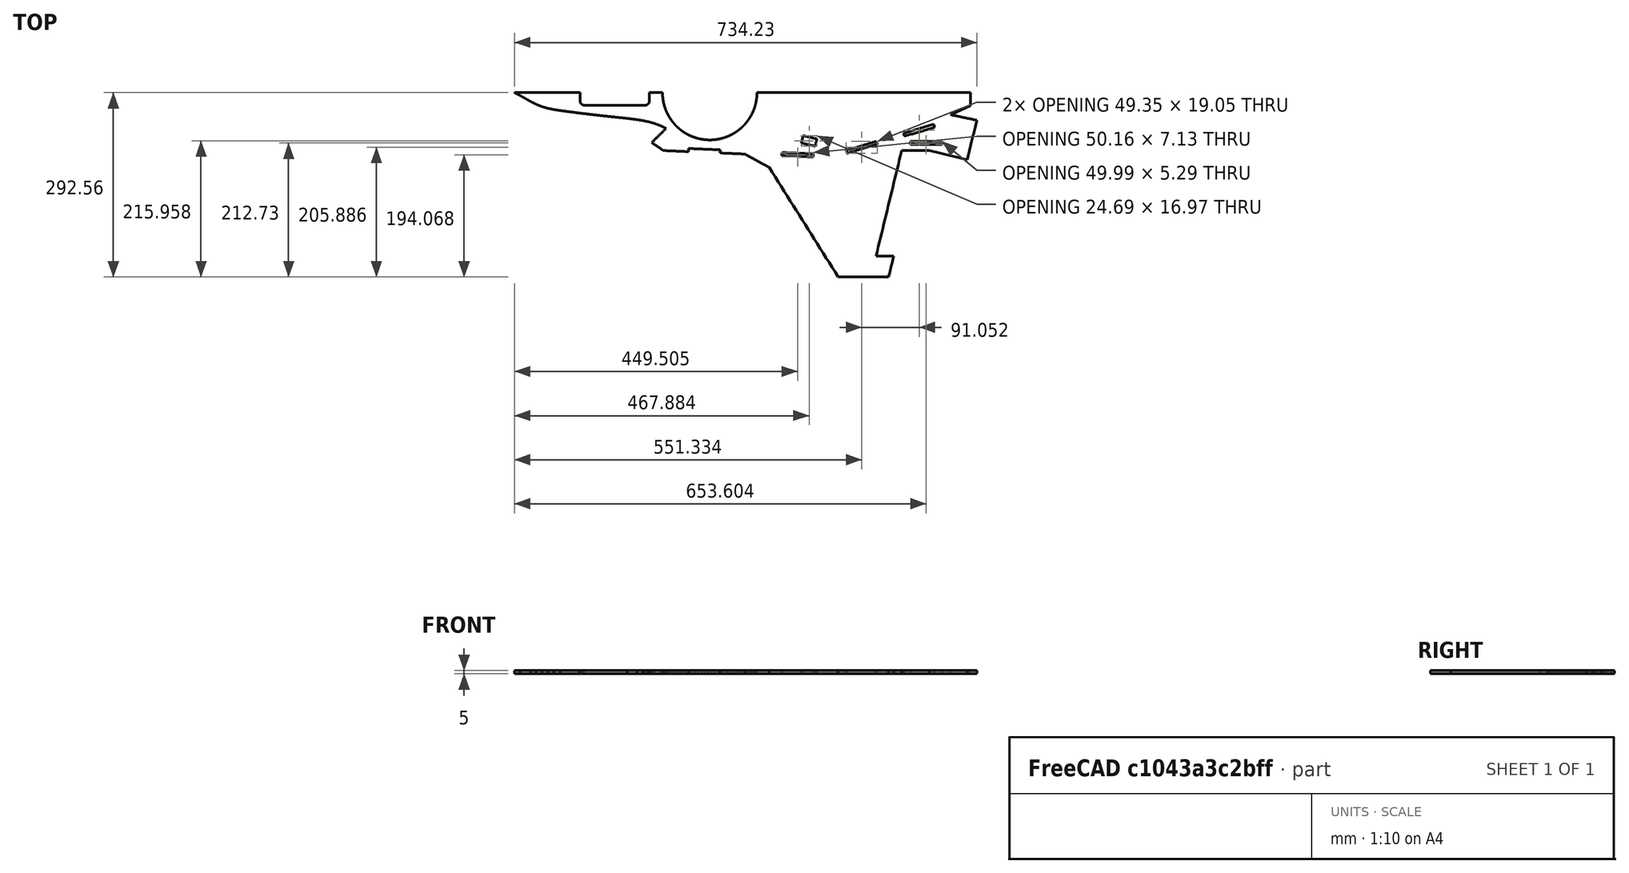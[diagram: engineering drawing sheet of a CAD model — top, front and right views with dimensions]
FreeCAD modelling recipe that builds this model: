
FCSTD DOCUMENT  (FreeCAD 0.19R)
Label: F-35_v2_parts_13
License: All rights reserved
LicenseURL: http://en.wikipedia.org/wiki/All_rights_reserved
objects: PartDesign::CoordinateSystem×7, App::DocumentObjectGroup×2, App::FeaturePython×1, Sketcher::SketchObject×1, PartDesign::Pad×1, PartDesign::Body×1, App::Part×1
note: 11 computed .brp shape members not serialized (recipe doc carries the construction recipe); baked Part::Feature solids carry a one-line shape summary decoded from their .brp

FEATURE [App::DocumentObjectGroup] Parts
FEATURE [PartDesign::CoordinateSystem] LCS_Origin
  AttacherType = Attacher::AttachEngine3D
  MapMode = 2
  Support = -> [X_Axis]
FEATURE [App::DocumentObjectGroup] Constraints
FEATURE [App::FeaturePython] Variables  # WARN: FeaturePython — macro-defined, semantics opaque (R4)
FEATURE [Sketcher::SketchObject] Sketch
  FullyConstrained = false
  sketch-geometry (125):
    g0: BSplineCurve PolesCount=2 KnotsCount=2 Degree=1 IsPeriodic=0
    g1: BSplineCurve PolesCount=2 KnotsCount=2 Degree=1 IsPeriodic=0
    g2: BSplineCurve PolesCount=2 KnotsCount=2 Degree=1 IsPeriodic=0
    g3: BSplineCurve PolesCount=2 KnotsCount=2 Degree=1 IsPeriodic=0
    g4: BSplineCurve PolesCount=2 KnotsCount=2 Degree=1 IsPeriodic=0
    g5: BSplineCurve PolesCount=2 KnotsCount=2 Degree=1 IsPeriodic=0
    g6: BSplineCurve PolesCount=2 KnotsCount=2 Degree=1 IsPeriodic=0
    g7: BSplineCurve PolesCount=2 KnotsCount=2 Degree=1 IsPeriodic=0
    g8: BSplineCurve PolesCount=2 KnotsCount=2 Degree=1 IsPeriodic=0
    g9: BSplineCurve PolesCount=2 KnotsCount=2 Degree=1 IsPeriodic=0
    g10: BSplineCurve PolesCount=2 KnotsCount=2 Degree=1 IsPeriodic=0
    g11: BSplineCurve PolesCount=2 KnotsCount=2 Degree=1 IsPeriodic=0
    g12: BSplineCurve PolesCount=2 KnotsCount=2 Degree=1 IsPeriodic=0
    g13: BSplineCurve PolesCount=2 KnotsCount=2 Degree=1 IsPeriodic=0
    g14: BSplineCurve PolesCount=2 KnotsCount=2 Degree=1 IsPeriodic=0
    g15: BSplineCurve PolesCount=2 KnotsCount=2 Degree=1 IsPeriodic=0
    g16: BSplineCurve PolesCount=2 KnotsCount=2 Degree=1 IsPeriodic=0
    g17: BSplineCurve PolesCount=2 KnotsCount=2 Degree=1 IsPeriodic=0
    g18: BSplineCurve PolesCount=2 KnotsCount=2 Degree=1 IsPeriodic=0
    g19: BSplineCurve PolesCount=2 KnotsCount=2 Degree=1 IsPeriodic=0
    g20: BSplineCurve PolesCount=2 KnotsCount=2 Degree=1 IsPeriodic=0
    g21: BSplineCurve PolesCount=2 KnotsCount=2 Degree=1 IsPeriodic=0
    g22: BSplineCurve PolesCount=2 KnotsCount=2 Degree=1 IsPeriodic=0
    g23: BSplineCurve PolesCount=2 KnotsCount=2 Degree=1 IsPeriodic=0
    g24: BSplineCurve PolesCount=2 KnotsCount=2 Degree=1 IsPeriodic=0
    g25: BSplineCurve PolesCount=2 KnotsCount=2 Degree=1 IsPeriodic=0
    g26: BSplineCurve PolesCount=2 KnotsCount=2 Degree=1 IsPeriodic=0
    g27: BSplineCurve PolesCount=2 KnotsCount=2 Degree=1 IsPeriodic=0
    g28: BSplineCurve PolesCount=2 KnotsCount=2 Degree=1 IsPeriodic=0
    g29: BSplineCurve PolesCount=2 KnotsCount=2 Degree=1 IsPeriodic=0
    g30: BSplineCurve PolesCount=2 KnotsCount=2 Degree=1 IsPeriodic=0
    g31: BSplineCurve PolesCount=2 KnotsCount=2 Degree=1 IsPeriodic=0
    g32: BSplineCurve PolesCount=2 KnotsCount=2 Degree=1 IsPeriodic=0
    g33: BSplineCurve PolesCount=2 KnotsCount=2 Degree=1 IsPeriodic=0
    g34: BSplineCurve PolesCount=2 KnotsCount=2 Degree=1 IsPeriodic=0
    g35: BSplineCurve PolesCount=2 KnotsCount=2 Degree=1 IsPeriodic=0
    g36: BSplineCurve PolesCount=2 KnotsCount=2 Degree=1 IsPeriodic=0
    g37: BSplineCurve PolesCount=2 KnotsCount=2 Degree=1 IsPeriodic=0
    g38: BSplineCurve PolesCount=2 KnotsCount=2 Degree=1 IsPeriodic=0
    g39: BSplineCurve PolesCount=2 KnotsCount=2 Degree=1 IsPeriodic=0
    g40: BSplineCurve PolesCount=2 KnotsCount=2 Degree=1 IsPeriodic=0
    g41: BSplineCurve PolesCount=2 KnotsCount=2 Degree=1 IsPeriodic=0
    g42: BSplineCurve PolesCount=2 KnotsCount=2 Degree=1 IsPeriodic=0
    g43: BSplineCurve PolesCount=2 KnotsCount=2 Degree=1 IsPeriodic=0
    g44: BSplineCurve PolesCount=2 KnotsCount=2 Degree=1 IsPeriodic=0
    g45: BSplineCurve PolesCount=2 KnotsCount=2 Degree=1 IsPeriodic=0
    g46: BSplineCurve PolesCount=2 KnotsCount=2 Degree=1 IsPeriodic=0
    g47: BSplineCurve PolesCount=2 KnotsCount=2 Degree=1 IsPeriodic=0
    g48: BSplineCurve PolesCount=2 KnotsCount=2 Degree=1 IsPeriodic=0
    g49: BSplineCurve PolesCount=2 KnotsCount=2 Degree=1 IsPeriodic=0
    g50: BSplineCurve PolesCount=2 KnotsCount=2 Degree=1 IsPeriodic=0
    g51: BSplineCurve PolesCount=2 KnotsCount=2 Degree=1 IsPeriodic=0
    g52: BSplineCurve PolesCount=2 KnotsCount=2 Degree=1 IsPeriodic=0
    g53: BSplineCurve PolesCount=2 KnotsCount=2 Degree=1 IsPeriodic=0
    g54: BSplineCurve PolesCount=2 KnotsCount=2 Degree=1 IsPeriodic=0
    g55: BSplineCurve PolesCount=2 KnotsCount=2 Degree=1 IsPeriodic=0
    g56: BSplineCurve PolesCount=2 KnotsCount=2 Degree=1 IsPeriodic=0
    g57: BSplineCurve PolesCount=2 KnotsCount=2 Degree=1 IsPeriodic=0
    g58: BSplineCurve PolesCount=2 KnotsCount=2 Degree=1 IsPeriodic=0
    g59: BSplineCurve PolesCount=2 KnotsCount=2 Degree=1 IsPeriodic=0
    g60: BSplineCurve PolesCount=2 KnotsCount=2 Degree=1 IsPeriodic=0
    g61: BSplineCurve PolesCount=2 KnotsCount=2 Degree=1 IsPeriodic=0
    g62: BSplineCurve PolesCount=2 KnotsCount=2 Degree=1 IsPeriodic=0
    g63: BSplineCurve PolesCount=2 KnotsCount=2 Degree=1 IsPeriodic=0
    g64: BSplineCurve PolesCount=2 KnotsCount=2 Degree=1 IsPeriodic=0
    g65: BSplineCurve PolesCount=2 KnotsCount=2 Degree=1 IsPeriodic=0
    g66: BSplineCurve PolesCount=2 KnotsCount=2 Degree=1 IsPeriodic=0
    g67: BSplineCurve PolesCount=2 KnotsCount=2 Degree=1 IsPeriodic=0
    g68: BSplineCurve PolesCount=2 KnotsCount=2 Degree=1 IsPeriodic=0
    g69: BSplineCurve PolesCount=2 KnotsCount=2 Degree=1 IsPeriodic=0
    g70: BSplineCurve PolesCount=2 KnotsCount=2 Degree=1 IsPeriodic=0
    g71: BSplineCurve PolesCount=2 KnotsCount=2 Degree=1 IsPeriodic=0
    g72: BSplineCurve PolesCount=2 KnotsCount=2 Degree=1 IsPeriodic=0
    g73: BSplineCurve PolesCount=2 KnotsCount=2 Degree=1 IsPeriodic=0
    g74: BSplineCurve PolesCount=2 KnotsCount=2 Degree=1 IsPeriodic=0
    g75: BSplineCurve PolesCount=2 KnotsCount=2 Degree=1 IsPeriodic=0
    g76: BSplineCurve PolesCount=2 KnotsCount=2 Degree=1 IsPeriodic=0
    g77: BSplineCurve PolesCount=2 KnotsCount=2 Degree=1 IsPeriodic=0
    g78: BSplineCurve PolesCount=2 KnotsCount=2 Degree=1 IsPeriodic=0
    g79: BSplineCurve PolesCount=2 KnotsCount=2 Degree=1 IsPeriodic=0
    g80: BSplineCurve PolesCount=2 KnotsCount=2 Degree=1 IsPeriodic=0
    g81: BSplineCurve PolesCount=2 KnotsCount=2 Degree=1 IsPeriodic=0
    g82: BSplineCurve PolesCount=2 KnotsCount=2 Degree=1 IsPeriodic=0
    g83: BSplineCurve PolesCount=2 KnotsCount=2 Degree=1 IsPeriodic=0
    g84: BSplineCurve PolesCount=2 KnotsCount=2 Degree=1 IsPeriodic=0
    g85: BSplineCurve PolesCount=2 KnotsCount=2 Degree=1 IsPeriodic=0
    g86: BSplineCurve PolesCount=2 KnotsCount=2 Degree=1 IsPeriodic=0
    g87: BSplineCurve PolesCount=2 KnotsCount=2 Degree=1 IsPeriodic=0
    g88: BSplineCurve PolesCount=2 KnotsCount=2 Degree=1 IsPeriodic=0
    g89: BSplineCurve PolesCount=2 KnotsCount=2 Degree=1 IsPeriodic=0
    g90: BSplineCurve PolesCount=2 KnotsCount=2 Degree=1 IsPeriodic=0
    g91: BSplineCurve PolesCount=2 KnotsCount=2 Degree=1 IsPeriodic=0
    g92: BSplineCurve PolesCount=2 KnotsCount=2 Degree=1 IsPeriodic=0
    g93: BSplineCurve PolesCount=2 KnotsCount=2 Degree=1 IsPeriodic=0
    g94: BSplineCurve PolesCount=2 KnotsCount=2 Degree=1 IsPeriodic=0
    g95: BSplineCurve PolesCount=2 KnotsCount=2 Degree=1 IsPeriodic=0
    g96: BSplineCurve PolesCount=2 KnotsCount=2 Degree=1 IsPeriodic=0
    g97: BSplineCurve PolesCount=2 KnotsCount=2 Degree=1 IsPeriodic=0
    g98: BSplineCurve PolesCount=2 KnotsCount=2 Degree=1 IsPeriodic=0
    g99: BSplineCurve PolesCount=2 KnotsCount=2 Degree=1 IsPeriodic=0
    g100: BSplineCurve PolesCount=2 KnotsCount=2 Degree=1 IsPeriodic=0
    g101: BSplineCurve PolesCount=2 KnotsCount=2 Degree=1 IsPeriodic=0
    g102: BSplineCurve PolesCount=2 KnotsCount=2 Degree=1 IsPeriodic=0
    g103: BSplineCurve PolesCount=2 KnotsCount=2 Degree=1 IsPeriodic=0
    g104: BSplineCurve PolesCount=2 KnotsCount=2 Degree=1 IsPeriodic=0
    g105: BSplineCurve PolesCount=2 KnotsCount=2 Degree=1 IsPeriodic=0
    g106: BSplineCurve PolesCount=2 KnotsCount=2 Degree=1 IsPeriodic=0
    g107: BSplineCurve PolesCount=2 KnotsCount=2 Degree=1 IsPeriodic=0
    g108: BSplineCurve PolesCount=2 KnotsCount=2 Degree=1 IsPeriodic=0
    g109: BSplineCurve PolesCount=2 KnotsCount=2 Degree=1 IsPeriodic=0
    g110: BSplineCurve PolesCount=2 KnotsCount=2 Degree=1 IsPeriodic=0
    g111: BSplineCurve PolesCount=2 KnotsCount=2 Degree=1 IsPeriodic=0
    g112: BSplineCurve PolesCount=2 KnotsCount=2 Degree=1 IsPeriodic=0
    g113: BSplineCurve PolesCount=2 KnotsCount=2 Degree=1 IsPeriodic=0
    g114: BSplineCurve PolesCount=2 KnotsCount=2 Degree=1 IsPeriodic=0
    g115: BSplineCurve PolesCount=2 KnotsCount=2 Degree=1 IsPeriodic=0
    g116: BSplineCurve PolesCount=2 KnotsCount=2 Degree=1 IsPeriodic=0
    g117: BSplineCurve PolesCount=2 KnotsCount=2 Degree=1 IsPeriodic=0
    g118: BSplineCurve PolesCount=2 KnotsCount=2 Degree=1 IsPeriodic=0
    g119: BSplineCurve PolesCount=2 KnotsCount=2 Degree=1 IsPeriodic=0
    g120: BSplineCurve PolesCount=2 KnotsCount=2 Degree=1 IsPeriodic=0
    g121: BSplineCurve PolesCount=2 KnotsCount=2 Degree=1 IsPeriodic=0
    g122: BSplineCurve PolesCount=2 KnotsCount=2 Degree=1 IsPeriodic=0
    g123: BSplineCurve PolesCount=2 KnotsCount=2 Degree=1 IsPeriodic=0
    g124: BSplineCurve PolesCount=2 KnotsCount=2 Degree=1 IsPeriodic=0
  constraints (76):
    c: Coincident(g20,g21)
    c: Coincident(g21,g22)
    c: Coincident(g22,g23)
    c: Coincident(g23,g24)
    c: Coincident(g24,g25)
    c: Coincident(g25,g26)
    c: Coincident(g26,g27)
    c: Coincident(g29,g30)
    c: Coincident(g30,g31)
    c: Coincident(g31,g32)
    c: Coincident(g32,g33)
    c: Coincident(g33,g34)
    c: Coincident(g34,g35)
    c: Coincident(g35,g36)
    c: Coincident(g39,g40)
    c: Coincident(g40,g41)
    c: Coincident(g41,g42)
    c: Coincident(g42,g43)
    c: Coincident(g43,g44)
    c: Coincident(g44,g45)
    c: Coincident(g45,g46)
    c: Coincident(g46,g47)
    c: Coincident(g47,g48)
    c: Coincident(g48,g49)
    c: Coincident(g49,g50)
    c: Coincident(g50,g51)
    c: Coincident(g51,g52)
    c: Coincident(g52,g53)
    c: Coincident(g53,g54)
    c: Coincident(g54,g55)
    c: Coincident(g55,g56)
    c: Coincident(g56,g57)
    c: Coincident(g57,g58)
    c: Coincident(g58,g59)
    c: Coincident(g59,g60)
    c: Coincident(g60,g61)
    c: Coincident(g61,g62)
    c: Coincident(g62,g63)
    c: Coincident(g63,g64)
    c: Coincident(g64,g65)
    c: Coincident(g65,g66)
    c: Coincident(g66,g67)
    c: Coincident(g67,g68)
    c: Coincident(g68,g69)
    c: Coincident(g69,g70)
    c: Coincident(g70,g71)
    c: Coincident(g71,g72)
    c: Coincident(g72,g73)
    c: Coincident(g73,g74)
    c: Coincident(g74,g75)
    c: Coincident(g75,g76)
    c: Coincident(g76,g77)
    c: Coincident(g77,g78)
    c: Coincident(g78,g79)
    c: Coincident(g79,g80)
    c: Coincident(g80,g81)
    c: Coincident(g81,g82)
    c: Coincident(g82,g83)
    c: Coincident(g103,g104)
    c: Coincident(g104,g105)
    c: Coincident(g105,g106)
    c: Coincident(g106,g107)
    c: Coincident(g107,g108)
    c: Coincident(g108,g109)
    c: Coincident(g109,g110)
    c: Coincident(g110,g111)
    c: Coincident(g111,g112)
    c: Coincident(g112,g113)
    c: Coincident(g113,g114)
    c: Coincident(g114,g115)
    c: Coincident(g115,g116)
    c: Coincident(g116,g117)
    c: Coincident(g117,g118)
    c: Coincident(g118,g119)
    c: Coincident(g119,g120)
    c: Coincident(g120,g121)
FEATURE [PartDesign::Pad] Pad006
  Direction = (1,1,1)
  Length = 5
  Length2 = 100
  Profile = -> Sketch
  Type = 0
FEATURE [PartDesign::Body] Body  label="Part13"
  Group = -> [Sketch,Pad006]
  Origin = -> Origin001
  Tip = -> Pad006
FEATURE [PartDesign::CoordinateSystem] LCS_1
  AttacherType = Attacher::AttachEngine3D
  MapMode = 7
  Placement = pos=(858.331,-105.427,0) rot=(0,1,0;3.14159rad)
  Support = -> [Pad006]
FEATURE [PartDesign::CoordinateSystem] LCS_2
  AttacherType = Attacher::AttachEngine3D
  MapMode = 7
  Placement = pos=(410.797,-194.009,5) rot=(0.014931,0.707028,0.707028;3.11173rad)
  Support = -> [Pad006]
FEATURE [PartDesign::CoordinateSystem] LCS_3
  AttacherType = Attacher::AttachEngine3D
  MapMode = 7
  Placement = pos=(660.987,-196.831,5) rot=(-0.101306,0.703469,0.703469;3.34352rad)
  Support = -> [Pad006]
FEATURE [PartDesign::CoordinateSystem] LCS_4
  AttacherType = Attacher::AttachEngine3D
  MapMode = 7
  Placement = pos=(749.005,-197.325,0) rot=(0.084189,0.704596,0.704596;2.97361rad)
  Support = -> [Pad006]
FEATURE [PartDesign::CoordinateSystem] LCS_5
  AttacherType = Attacher::AttachEngine3D
  MapMode = 7
  Placement = pos=(852.898,-211.824,0) rot=(0.985165,-0.121346,-0.121346;1.58574rad)
  Support = -> [Pad006]
FEATURE [PartDesign::CoordinateSystem] LCS_6
  AttacherType = Attacher::AttachEngine3D
  MapMode = 45
  Placement = pos=(812.929,-185.401,2.5) rot=(0.707107,0,0.707107;3.14159rad)
  Support = -> [Pad006]
FEATURE [App::Part] Model
  Configuration = 0
  Group = -> [LCS_Origin,Constraints,Variables,Body,LCS_1,LCS_2,LCS_3,LCS_4,LCS_5,LCS_6]
  Origin = -> Origin
  Type = Assembly4 Model
